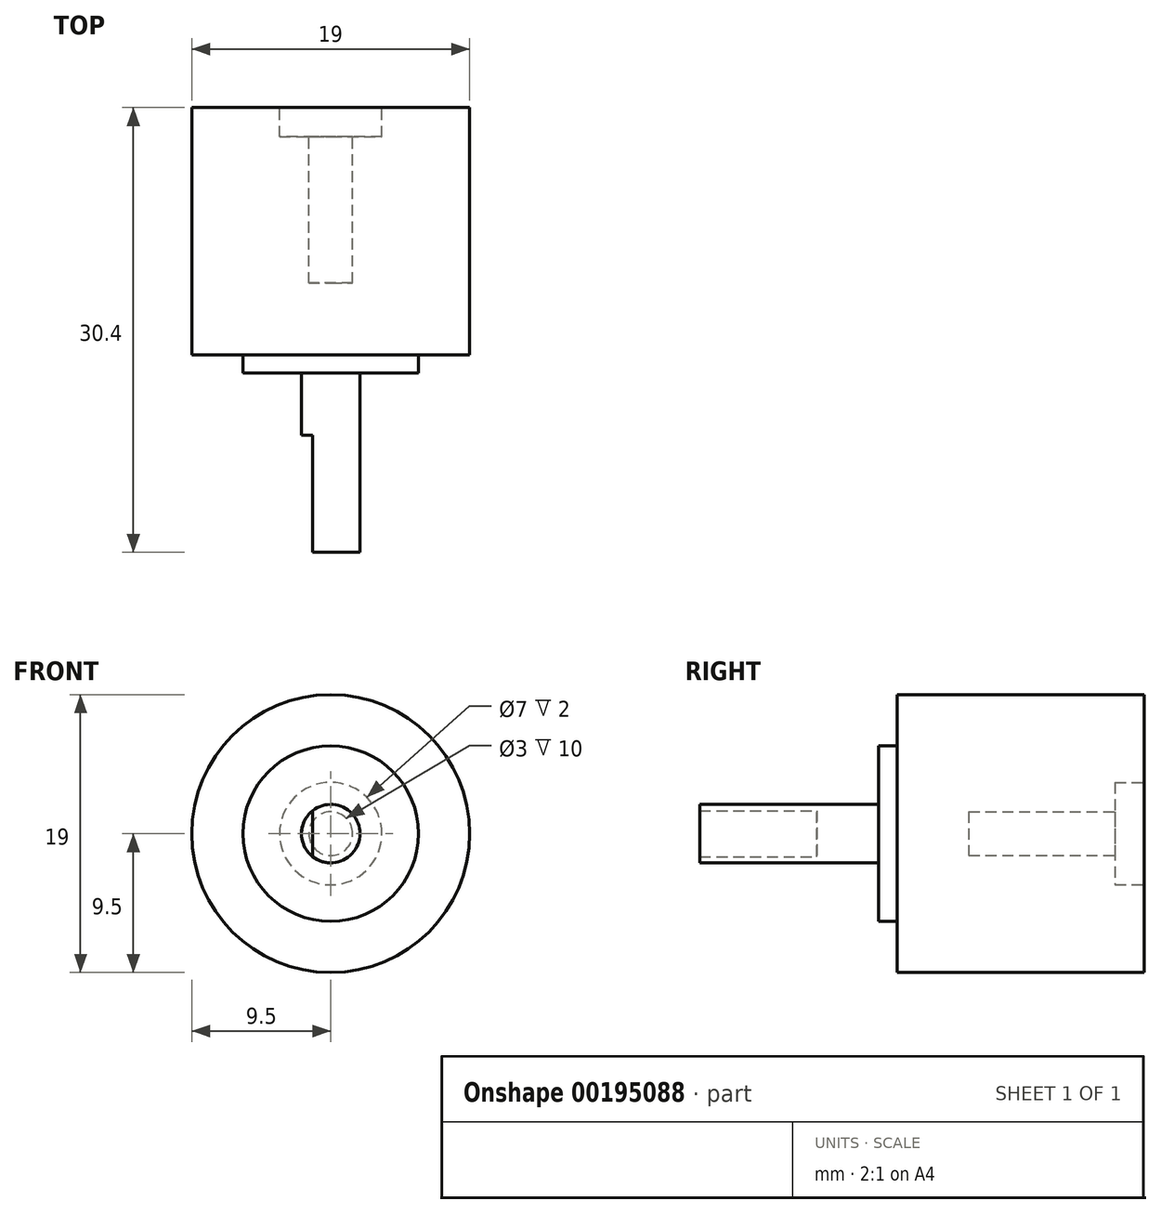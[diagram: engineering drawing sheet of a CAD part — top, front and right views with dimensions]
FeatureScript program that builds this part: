
annotation { "Feature Type Name" : "Feature", "Feature Type Description" : "" }
export const myFeature = defineFeature(function(context is Context, id is Id, definition is map)
    precondition{}
    {
        {
            var Q0;
            Q0=qCreatedBy(makeId("Front.planeOp"),FACE);
            var sketch = newSketch(context, id + "F0", { "sketchPlane" : qUnion([Q0])});
            skCircle(sketch, "E0", {"center": v(0, 0) * mm, "radius": 9.5 * mm});
            skSolve(sketch);
        }
        {
            var Q0;
            Q0 = qSketchRegion(id + "F0", true);
            extrude(context, id + "F1", {"entities" : qUnion([Q0]), "depth" : 16.9 * mm});
        }
        {
            var Q0;
            Q0=makeQuery(id+"F1.opExtrude","CAP_FACE",FACE,{"disambiguationData":[OSD([sQuery(id+"F0.wireOp",EDGE,"E0")])],"isStart":false});
            var sketch = newSketch(context, id + "F2", { "sketchPlane" : qUnion([Q0])});
            skCircle(sketch, "E1", {"center": v(0, 0) * mm, "radius": 6 * mm});
            skSolve(sketch);
        }
        {
            var Q0;
            Q0 = qSketchRegion(id + "F2", true);
            extrude(context, id + "F3", {"entities" : qUnion([Q0]), "operationType" : NewBodyOperationType.ADD, "depth" : 1.25 * mm});
        }
        {
            var Q0;
            Q0=makeQuery(id+"F3.opExtrude","CAP_FACE",FACE,{"disambiguationData":[OSD([sQuery(id+"F2.wireOp",EDGE,"E1")])],"isStart":false});
            var sketch = newSketch(context, id + "F4", { "sketchPlane" : qUnion([Q0])});
            skCircle(sketch, "E2", {"center": v(0, 0) * mm, "radius": 2 * mm});
            skSolve(sketch);
        }
        {
            var Q0;
            Q0 = qSketchRegion(id + "F4", true);
            extrude(context, id + "F5", {"entities" : qUnion([Q0]), "operationType" : NewBodyOperationType.ADD, "depth" : 12.25 * mm});
        }
        {
            var Q0;
            Q0=makeQuery(id+"F5.opExtrude","CAP_FACE",FACE,{"disambiguationData":[OSD([sQuery(id+"F4.wireOp",EDGE,"E2")])],"isStart":false});
            var sketch = newSketch(context, id + "F6", { "sketchPlane" : qUnion([Q0])});
            skLineSegment(sketch, "E3.bottom", {"start": v(-1.24, -2.72) * mm, "end": v(-2.76, -2.72) * mm});
            skLineSegment(sketch, "E3.top", {"start": v(-1.24, 3.02) * mm, "end": v(-2.76, 3.02) * mm});
            skLineSegment(sketch, "E3.left", {"start": v(-1.24, -2.72) * mm, "end": v(-1.24, 3.02) * mm});
            skLineSegment(sketch, "E3.right", {"start": v(-2.76, -2.72) * mm, "end": v(-2.76, 3.02) * mm});
            skSolve(sketch);
        }
        {
            var Q0;
            Q0 = qSketchRegion(id + "F6", true);
            extrude(context, id + "F7", {"entities" : qUnion([Q0]), "operationType" : NewBodyOperationType.REMOVE, "oppositeDirection" : true, "depth" : 8 * mm});
        }
        {
            var Q0;
            Q0=makeQuery(id+"F1.opExtrude","CAP_FACE",FACE,{"disambiguationData":[OSD([sQuery(id+"F0.wireOp",EDGE,"E0")])],"isStart":true});
            var sketch = newSketch(context, id + "F8", { "sketchPlane" : qUnion([Q0])});
            skCircle(sketch, "E4", {"center": v(0, 0) * mm, "radius": 3.5 * mm});
            skSolve(sketch);
        }
        {
            var Q0;
            Q0 = qSketchRegion(id + "F8", true);
            extrude(context, id + "F9", {"entities" : qUnion([Q0]), "operationType" : NewBodyOperationType.REMOVE, "oppositeDirection" : true, "depth" : 2 * mm});
        }
        {
            var Q0;
            Q0=makeQuery(id+"F9.boolean.opBoolean","COPY",FACE,{"derivedFrom":makeQuery(id+"F9.opExtrude","CAP_FACE",FACE,{"disambiguationData":[OSD([sQuery(id+"F8.wireOp",EDGE,"E4")])],"isStart":false})});
            var sketch = newSketch(context, id + "F10", { "sketchPlane" : qUnion([Q0])});
            skCircle(sketch, "E5", {"center": v(0, 0) * mm, "radius": 1.5 * mm});
            skSolve(sketch);
        }
        {
            var Q0;
            Q0 = qSketchRegion(id + "F10", true);
            extrude(context, id + "F11", {"entities" : qUnion([Q0]), "operationType" : NewBodyOperationType.REMOVE, "oppositeDirection" : true, "depth" : 10 * mm});
        }
    });
